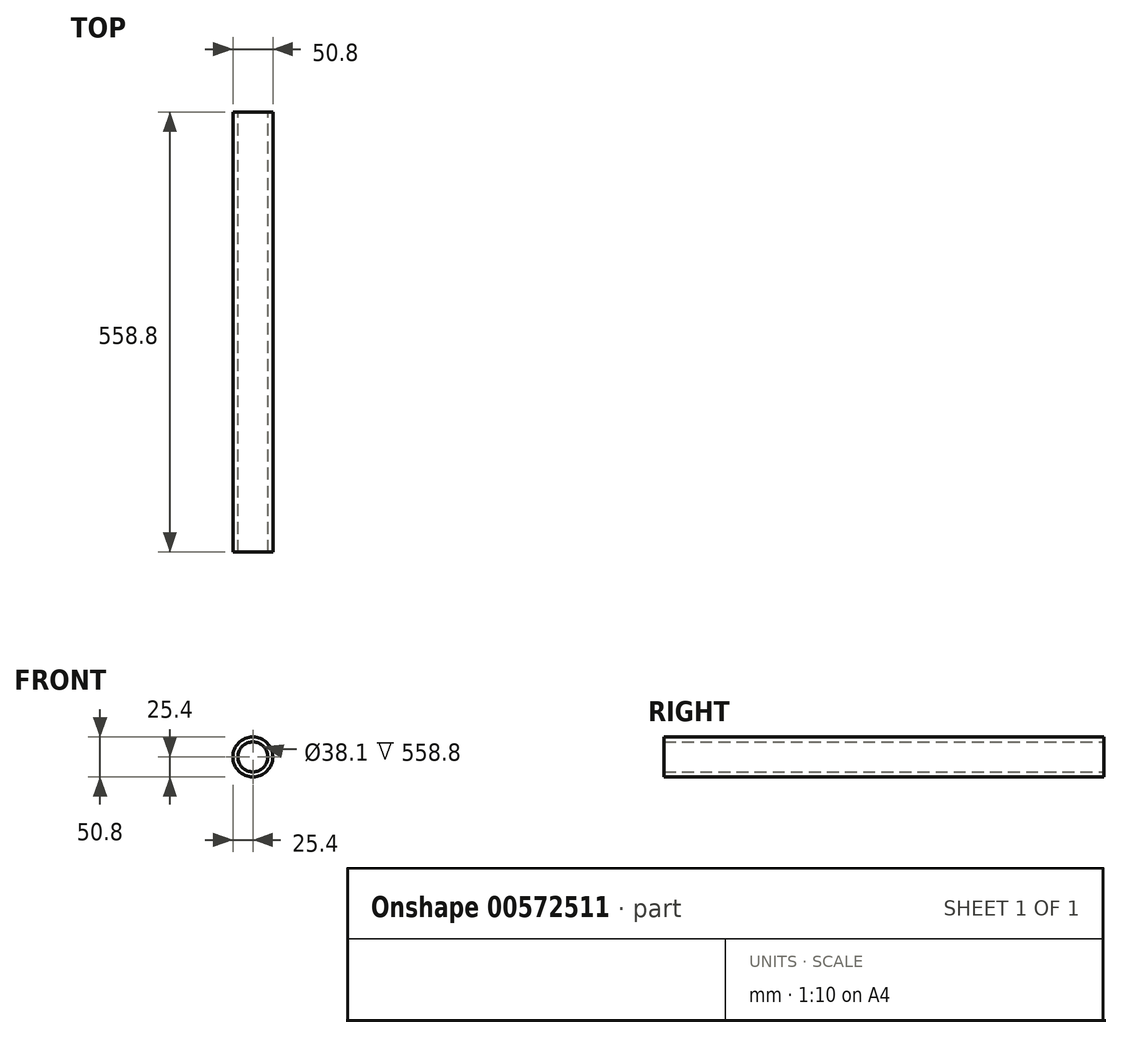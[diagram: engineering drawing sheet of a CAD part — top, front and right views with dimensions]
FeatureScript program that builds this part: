
annotation { "Feature Type Name" : "Feature", "Feature Type Description" : "" }
export const myFeature = defineFeature(function(context is Context, id is Id, definition is map)
    precondition{}
    {
        {
            var Q0;
            Q0=qCreatedBy(makeId("Front.planeOp"),FACE);
            var sketch = newSketch(context, id + "F0", { "sketchPlane" : qUnion([Q0])});
            skCircle(sketch, "E0", {"center": v(0, 0) * mm, "radius": 25.4 * mm});
            skCircle(sketch, "E1", {"center": v(0, 0) * mm, "radius": 19.05 * mm});
            skSolve(sketch);
        }
        {
            var Q0;
            Q0 = qSketchRegion(id + "F0", true);
            extrude(context, id + "F1", {"entities" : qUnion([Q0]), "depth" : 558.8 * mm, "offsetDistance" : 25.4 * mm});
        }
    });
